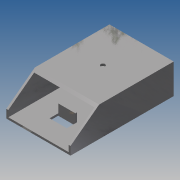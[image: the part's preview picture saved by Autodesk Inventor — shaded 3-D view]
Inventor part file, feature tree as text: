
AUTODESK INVENTOR PART (.ipt)
format: ipt  version: 2014 SP1 (Build 180222100, 222)  size: 137,728 bytes
history: native  units: in
note: dims shown in document units (in); Inventor stores cm internally (conversion verified against a paired STEP export)
features: sketch x6, extrude x4, hole x2, plane x1
ambient origin geometry x8: Origin, YZ Plane, XZ Plane, XY Plane, X Axis, Y Axis, Z Axis, Center Point
bodies: Solid1 (feature_tree)
feature tree (13):
  extrude  "Extrusion1"  Depth=1.5in
  plane  "Work Plane1"
  extrude  "Extrusion2"  Depth=6.0in TaperAngle=0.0deg
  extrude  "Extrusion4"  Depth=1.0in TaperAngle=0.0deg
  extrude  "Extrusion5"  Depth=1.0in
  hole  "holePair"  [1 undecoded]
  hole  "Hole5"  [1 undecoded]
  sketch  "Sketch1"  dims[d0=3.5in d1=1.5in]
  sketch  "Sketch2"  dims[d2=0.12in d3=6.0in d4=0.0in]
  sketch  "Sketch5"  dims[d5=-0.2542in d6=1.0in d7=0.0in]
  sketch  "Sketch7"  dims[d8=5.0in d21=1.0in]
  sketch  "Sketch9"  dims[d22=0.1in d23=1.75in]
  sketch  "Sketch10"  dims[d24=1.25in d25=0.5in d26=0.0in d36=0.5in d37=1.0in d38=0.0in d39=1.0in d40=0.0in d59=0.25in d60=0.75in d61=0.87in d62=0.25in d63=2.0in d67=0.25in d68=0.75in d69=0.375in d70=0.25in d71=0.5635in d72=1.0in d73=0.8108in d74=1.5in d75=0.25in d76=0.75in d77=0.375in d78=0.25in d79=0.5635in d80=1.0in d81=0.8108in]
note: 2 required parameter values undecoded (feature->parameter linkage not recoverable at this tier; creation-order binding heuristic only, values carry confidence <= 0.55)
